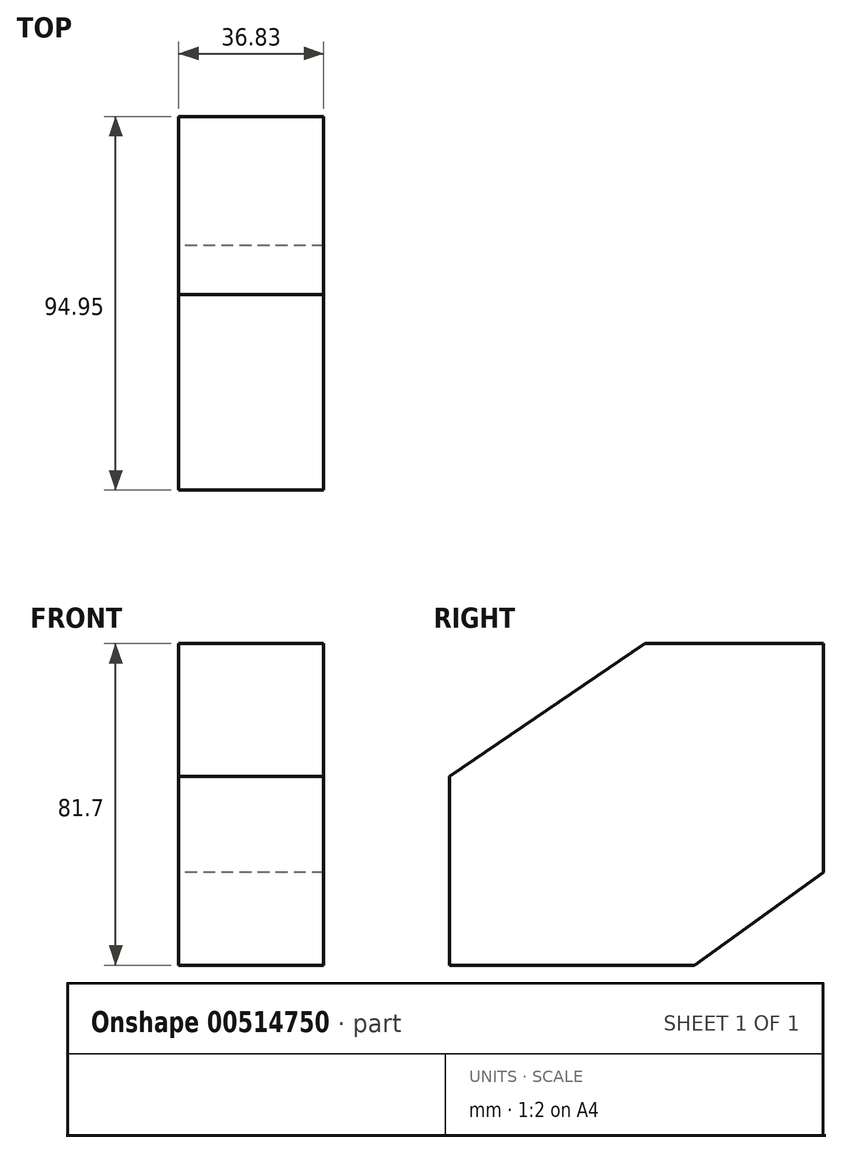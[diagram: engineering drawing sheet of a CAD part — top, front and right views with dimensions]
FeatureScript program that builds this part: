
annotation { "Feature Type Name" : "Feature", "Feature Type Description" : "" }
export const myFeature = defineFeature(function(context is Context, id is Id, definition is map)
    precondition{}
    {
        {
            var Q0;
            Q0=qCreatedBy(makeId("Right.planeOp"),FACE);
            var sketch = newSketch(context, id + "F0", { "sketchPlane" : qUnion([Q0])});
            skLineSegment(sketch, "E0.bottom", {"start": v(-44.34, 40.25) * mm, "end": v(50.6, 40.25) * mm});
            skLineSegment(sketch, "E0.top", {"start": v(-44.34, -41.45) * mm, "end": v(50.6, -41.45) * mm});
            skLineSegment(sketch, "E0.left", {"start": v(-44.34, 40.25) * mm, "end": v(-44.34, -41.45) * mm});
            skLineSegment(sketch, "E0.right", {"start": v(50.6, 40.25) * mm, "end": v(50.6, -41.45) * mm});
            skLineSegment(sketch, "E1", {"start": v(-44.34, 6.5) * mm, "end": v(5.3, 40.25) * mm});
            skLineSegment(sketch, "E2", {"start": v(50.6, -17.83) * mm, "end": v(17.83, -41.45) * mm});
            skSolve(sketch);
        }
        {
            var Q0;
            {var subQ3=sQuery(id+"F0.wireOp",EDGE,"E1");Q0=makeQuery(id+"F0.imprint","IMPRINT",FACE,{"disambiguationData":[TD([[makeQuery(id+"F0.imprint","IMPRINT",EDGE,{"derivedFrom":subQ3}),-1.0]])]});}
            extrude(context, id + "F1", {"entities" : qUnion([Q0]), "depth" : 36.83 * mm, "offsetDistance" : 25.4 * mm});
        }
    });
